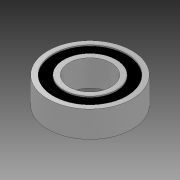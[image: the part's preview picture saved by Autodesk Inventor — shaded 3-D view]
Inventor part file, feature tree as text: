
AUTODESK INVENTOR PART (.ipt)
format: ipt  version: 2022 (Build 260153000, 153)  size: 136,192 bytes
history: native  units: mm
features: revolve x1, sketch x1
ambient origin geometry x8: Origin, YZ Plane, XZ Plane, XY Plane, X Axis, Y Axis, Z Axis, Center Point
bodies: Solid1 (feature_tree)
feature tree (2):
  revolve  "Revolution1"  [1 undecoded]
  sketch  "Sketch1"  dims[d0=4.0mm d2=5.0mm d5=8.0mm d6=0.2mm d7=1.0mm d8=90.0deg]
note: 1 required parameter value undecoded (feature->parameter linkage not recoverable at this tier; creation-order binding heuristic only, values carry confidence <= 0.55)
